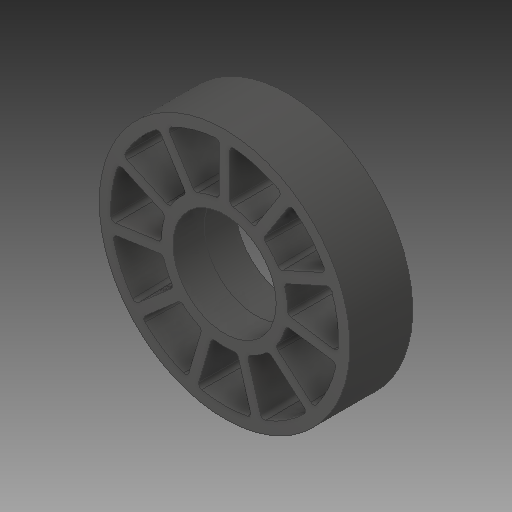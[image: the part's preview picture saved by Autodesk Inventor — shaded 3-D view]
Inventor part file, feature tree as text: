
AUTODESK INVENTOR PART (.ipt)
format: ipt  version: 2019 (Build 230136000, 136)  size: 369,664 bytes
history: native  units: in
note: dims shown in document units (in); Inventor stores cm internally (conversion verified against a paired STEP export)
features: fillet x1
ambient origin geometry x8: Origin, YZ Plane, XZ Plane, XY Plane, X Axis, Y Axis, Z Axis, Center Point
bodies: Solid1 (feature_tree)
feature tree (1):
  fillet  "Fillet1"  [1 undecoded]
note: 1 required parameter value undecoded (feature->parameter linkage not recoverable at this tier; creation-order binding heuristic only, values carry confidence <= 0.55)
